# Revit family: CN4
name_source: partatom
category: Lighting Fixtures
revit_build: Autodesk Revit Architecture 2012 (Build: 20110309_2315(x64)
units: mm (PartAtom-declared; Revit-internal decimal feet)

## types (1)
- CN4-254-EP-PAF
    Backbox = White
    Ballast = PAV254T5M
    Color Filter = 16777215
    Default Elevation = 48.000"
    Description = Narrow strip designed specifically for T5/T5HO applications offers smallest strip luminaire for coves, indirect lighting and other restricted spaces that require high performance.
    Dimming Lamp Color Temperature Shift = <None>
    Emit from Line Length = 24.000"
    Glass = Glass
    Lamp = F54T5
    Manufacturer = Columbia Lighting
    Manufacturer Fax = 866-898-1065
    Model = CN4
    Photometric Web File = 12789.IES
    Product Documentation Link = http://www.columbialighting.com
    Product Page URL = http://www.columbialighting.com
    Tilt Angle = -90.00°
    URL = http://www.columbialighting.com
    Wattage Comments = 129 W

## geometry (parser evidence)
native form markers: Sweep x1
no freeform markers — native parametric forms only
